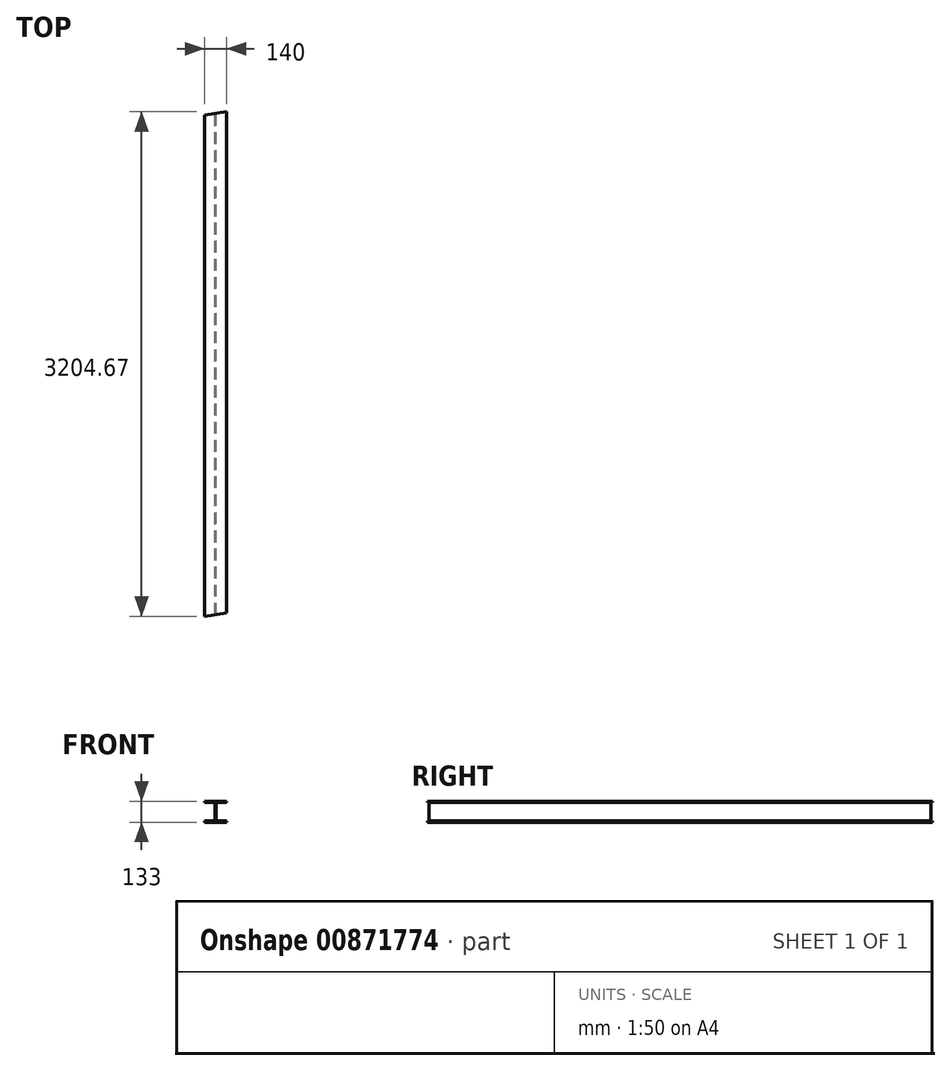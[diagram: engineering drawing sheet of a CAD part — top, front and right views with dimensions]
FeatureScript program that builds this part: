
annotation { "Feature Type Name" : "Feature", "Feature Type Description" : "" }
export const myFeature = defineFeature(function(context is Context, id is Id, definition is map)
    precondition{}
    {
        {
            var Q0;
            Q0=qCreatedBy(makeId("Front.planeOp"),FACE);
            var sketch = newSketch(context, id + "F0", { "sketchPlane" : qUnion([Q0])});
            skLineSegment(sketch, "E0.bottom", {"start": v(-90.22, -38.64) * mm, "end": v(49.78, -38.64) * mm});
            skLineSegment(sketch, "E0.top", {"start": v(-90.22, -30.14) * mm, "end": v(-34.97, -30.14) * mm});
            skLineSegment(sketch, "E0.left", {"start": v(-90.22, -38.64) * mm, "end": v(-90.22, -30.14) * mm});
            skLineSegment(sketch, "E0.right", {"start": v(49.78, -38.64) * mm, "end": v(49.78, -30.14) * mm});
            skLineSegment(sketch, "E1.left", {"start": v(-22.97, -18.14) * mm, "end": v(-22.97, 73.86) * mm});
            skLineSegment(sketch, "E1.right", {"start": v(-17.47, -18.14) * mm, "end": v(-17.47, 73.86) * mm});
            skLineSegment(sketch, "E2.bottom", {"start": v(-90.22, 85.86) * mm, "end": v(-34.97, 85.86) * mm});
            skLineSegment(sketch, "E2.top", {"start": v(-90.22, 94.36) * mm, "end": v(49.78, 94.36) * mm});
            skLineSegment(sketch, "E2.left", {"start": v(-90.22, 85.86) * mm, "end": v(-90.22, 94.36) * mm});
            skLineSegment(sketch, "E2.right", {"start": v(49.78, 85.86) * mm, "end": v(49.78, 94.36) * mm});
            skArc(sketch, "E3.filletArc", {"start": v(-22.97, 73.86) * mm, "mid": v(-26.48, 82.35) * mm, "end": v(-34.97, 85.86) * mm});
            skPoint(sketch, "E4.newPointB", {"position": v(49.78, -30.14) * mm});
            skArc(sketch, "E4.filletArc", {"start": v(-34.97, -30.14) * mm, "mid": v(-26.48, -26.62) * mm, "end": v(-22.97, -18.14) * mm});
            skLineSegment(sketch, "E5", {"start": v(-5.47, 85.86) * mm, "end": v(49.78, 85.86) * mm});
            skLineSegment(sketch, "E6", {"start": v(49.78, -30.14) * mm, "end": v(-5.47, -30.14) * mm});
            skPoint(sketch, "E7.visualSharp", {"position": v(-17.47, 85.86) * mm});
            skArc(sketch, "E7.filletArc", {"start": v(-5.47, 85.86) * mm, "mid": v(-13.96, 82.35) * mm, "end": v(-17.47, 73.86) * mm});
            skPoint(sketch, "E8.visualSharp", {"position": v(-17.47, -30.14) * mm});
            skArc(sketch, "E8.filletArc", {"start": v(-17.47, -18.14) * mm, "mid": v(-13.96, -26.62) * mm, "end": v(-5.47, -30.14) * mm});
            skSolve(sketch);
        }
        {
            var Q0;
            Q0 = qSketchRegion(id + "F0", true);
            extrude(context, id + "F1", {"entities" : qUnion([Q0]), "depth" : 4170 * mm, "offsetDistance" : 25 * mm});
        }
        {
            var Q0;
            Q0=makeQuery(id+"F1.opExtrude","SWEPT_FACE",FACE,{"disambiguationData":[OSD([sQuery(id+"F0.wireOp",EDGE,"E2.top")])]});
            var sketch = newSketch(context, id + "F2", { "sketchPlane" : qUnion([Q0])});
            skLineSegment(sketch, "E9", {"start": v(-90.22, -4170) * mm, "end": v(1890.32, -3891.65) * mm});
            skLineSegment(sketch, "E10", {"start": v(1890.32, -3891.65) * mm, "end": v(1890.32, -4170) * mm});
            skLineSegment(sketch, "E11", {"start": v(1890.32, -4170) * mm, "end": v(-90.22, -4170) * mm});
            skLineSegment(sketch, "E12", {"start": v(-90.22, -4170) * mm, "end": v(-529.17, -1046.7) * mm});
            skLineSegment(sketch, "E13", {"start": v(-529.17, -1046.7) * mm, "end": v(-309.45, -1015.82) * mm});
            skLineSegment(sketch, "E14", {"start": v(1890.32, -3891.65) * mm, "end": v(-529.17, 13323.9) * mm});
            skLineSegment(sketch, "E15", {"start": v(-309.45, -1015.82) * mm, "end": v(1451.36, -768.35) * mm});
            skLineSegment(sketch, "E16", {"start": v(1451.36, -768.35) * mm, "end": v(1208.1, 962.6) * mm});
            skLineSegment(sketch, "E17", {"start": v(1208.1, 962.6) * mm, "end": v(-529.17, 718.44) * mm});
            skLineSegment(sketch, "E18", {"start": v(-529.17, 718.44) * mm, "end": v(-529.17, -1046.7) * mm});
            skSolve(sketch);
        }
        {
            var Q0;
            {var subQ0=sQuery(id+"F2.wireOp",EDGE,"E11");var subQ2=sQuery(id+"F0.wireOp",EDGE,"E2.top");var subQ4=makeQuery(id+"F1.opExtrude","SWEPT_EDGE",EDGE,{"disambiguationData":[OSD([subQ2,sQuery(id+"F0.wireOp",EDGE,"E2.right")])]});var subQ6=makeQuery(id+"F2.imprint","INTERSECT",VERTEX,{"derivedFrom":[subQ4,subQ0]});Q0=makeQuery(id+"F2.imprint","IMPRINT",FACE,{"disambiguationData":[TD([[makeQuery(id+"F2.imprint","IMPRINT",EDGE,{"disambiguationData":[TD([[subQ6,-1.0]])],"derivedFrom":subQ4}),1.0]])]});}
            var Q1;
            {var subQ1=sQuery(id+"F0.wireOp",EDGE,"E2.top");var subQ6=makeQuery(id+"F1.opExtrude","CAP_EDGE",EDGE,{"disambiguationData":[OSD([subQ1])],"isStart":true});Q1=makeQuery(id+"F2.imprint","IMPRINT",FACE,{"disambiguationData":[TD([[makeQuery(id+"F2.imprint","IMPRINT",EDGE,{"derivedFrom":subQ6}),-1.0]])]});}
            extrude(context, id + "F3", {"entities" : qUnion([Q0, Q1]), "operationType" : NewBodyOperationType.REMOVE, "oppositeDirection" : true, "depth" : 200 * mm, "offsetDistance" : 25 * mm});
        }
    });
